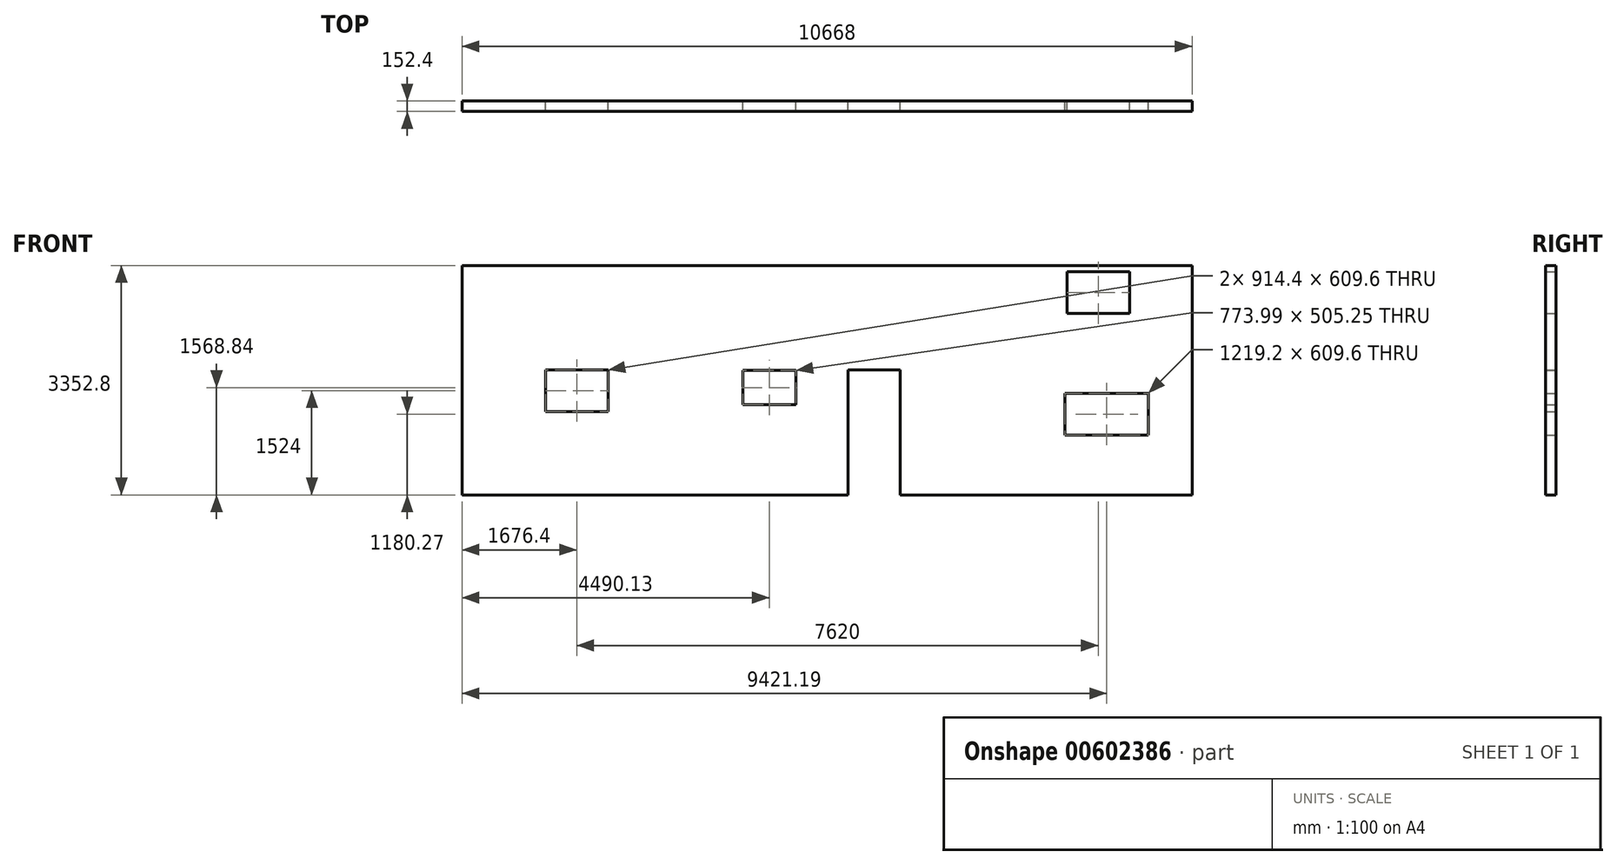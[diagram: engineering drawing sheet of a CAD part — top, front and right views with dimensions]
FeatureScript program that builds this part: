
annotation { "Feature Type Name" : "Feature", "Feature Type Description" : "" }
export const myFeature = defineFeature(function(context is Context, id is Id, definition is map)
    precondition{}
    {
        {
            var Q0;
            Q0=qCreatedBy(makeId("Front.planeOp"),FACE);
            var sketch = newSketch(context, id + "F0", { "sketchPlane" : qUnion([Q0])});
            skLineSegment(sketch, "E0.bottom", {"start": v(-5334, 1676.4) * mm, "end": v(5334, 1676.4) * mm});
            skLineSegment(sketch, "E0.top", {"start": v(-5334, -1676.4) * mm, "end": v(5334, -1676.4) * mm});
            skLineSegment(sketch, "E0.left", {"start": v(-5334, 1676.4) * mm, "end": v(-5334, -1676.4) * mm});
            skLineSegment(sketch, "E0.right", {"start": v(5334, 1676.4) * mm, "end": v(5334, -1676.4) * mm});
            skPoint(sketch, "E0.middle", {"position": v(0, 0) * mm});
            skLineSegment(sketch, "E1.bottom", {"start": v(-4114.8, 152.4) * mm, "end": v(-3200.4, 152.4) * mm});
            skLineSegment(sketch, "E1.top", {"start": v(-4114.8, -457.2) * mm, "end": v(-3200.4, -457.2) * mm});
            skLineSegment(sketch, "E1.left", {"start": v(-4114.8, 152.4) * mm, "end": v(-4114.8, -457.2) * mm});
            skLineSegment(sketch, "E1.right", {"start": v(-3200.4, 152.4) * mm, "end": v(-3200.4, -457.2) * mm});
            skPoint(sketch, "E1.middle", {"position": v(-3657.6, -152.4) * mm});
            skLineSegment(sketch, "E2.bottom", {"start": v(3505.2, 1584.96) * mm, "end": v(4419.6, 1584.96) * mm});
            skLineSegment(sketch, "E2.top", {"start": v(3505.2, 975.36) * mm, "end": v(4419.6, 975.36) * mm});
            skLineSegment(sketch, "E2.left", {"start": v(3505.2, 1584.96) * mm, "end": v(3505.2, 975.36) * mm});
            skLineSegment(sketch, "E2.right", {"start": v(4419.6, 1584.96) * mm, "end": v(4419.6, 975.36) * mm});
            skPoint(sketch, "E2.middle", {"position": v(3962.4, 1280.16) * mm});
            skLineSegment(sketch, "E3.bottom", {"start": v(304.8, -1676.4) * mm, "end": v(1066.8, -1676.4) * mm});
            skLineSegment(sketch, "E3.top", {"start": v(304.8, 152.4) * mm, "end": v(1066.8, 152.4) * mm});
            skLineSegment(sketch, "E3.left", {"start": v(304.8, -1676.4) * mm, "end": v(304.8, 152.4) * mm});
            skLineSegment(sketch, "E3.right", {"start": v(1066.8, -1676.4) * mm, "end": v(1066.8, 152.4) * mm});
            skLineSegment(sketch, "E4.bottom", {"start": v(3477.6, -191.33) * mm, "end": v(4696.8, -191.33) * mm});
            skLineSegment(sketch, "E4.top", {"start": v(3477.6, -800.93) * mm, "end": v(4696.8, -800.93) * mm});
            skLineSegment(sketch, "E4.left", {"start": v(3477.6, -191.33) * mm, "end": v(3477.6, -800.93) * mm});
            skLineSegment(sketch, "E4.right", {"start": v(4696.8, -191.33) * mm, "end": v(4696.8, -800.93) * mm});
            skLineSegment(sketch, "E5.bottom", {"start": v(-1230.86, 145.06) * mm, "end": v(-456.87, 145.06) * mm});
            skLineSegment(sketch, "E5.top", {"start": v(-1230.86, -360.18) * mm, "end": v(-456.87, -360.18) * mm});
            skLineSegment(sketch, "E5.left", {"start": v(-1230.86, 145.06) * mm, "end": v(-1230.86, -360.18) * mm});
            skLineSegment(sketch, "E5.right", {"start": v(-456.87, 145.06) * mm, "end": v(-456.87, -360.18) * mm});
            skSolve(sketch);
        }
        {
            var Q0;
            Q0=makeQuery(id+"F0.imprint","IMPRINT",FACE,{"disambiguationData":[TD([[makeQuery(id+"F0.imprint","IMPRINT",EDGE,{"derivedFrom":sQuery(id+"F0.wireOp",EDGE,"E0.bottom")}),-1.0]])]});
            extrude(context, id + "F1", {"entities" : qUnion([Q0]), "depth" : 152.4 * mm, "offsetDistance" : 30.48 * mm});
        }
    });
